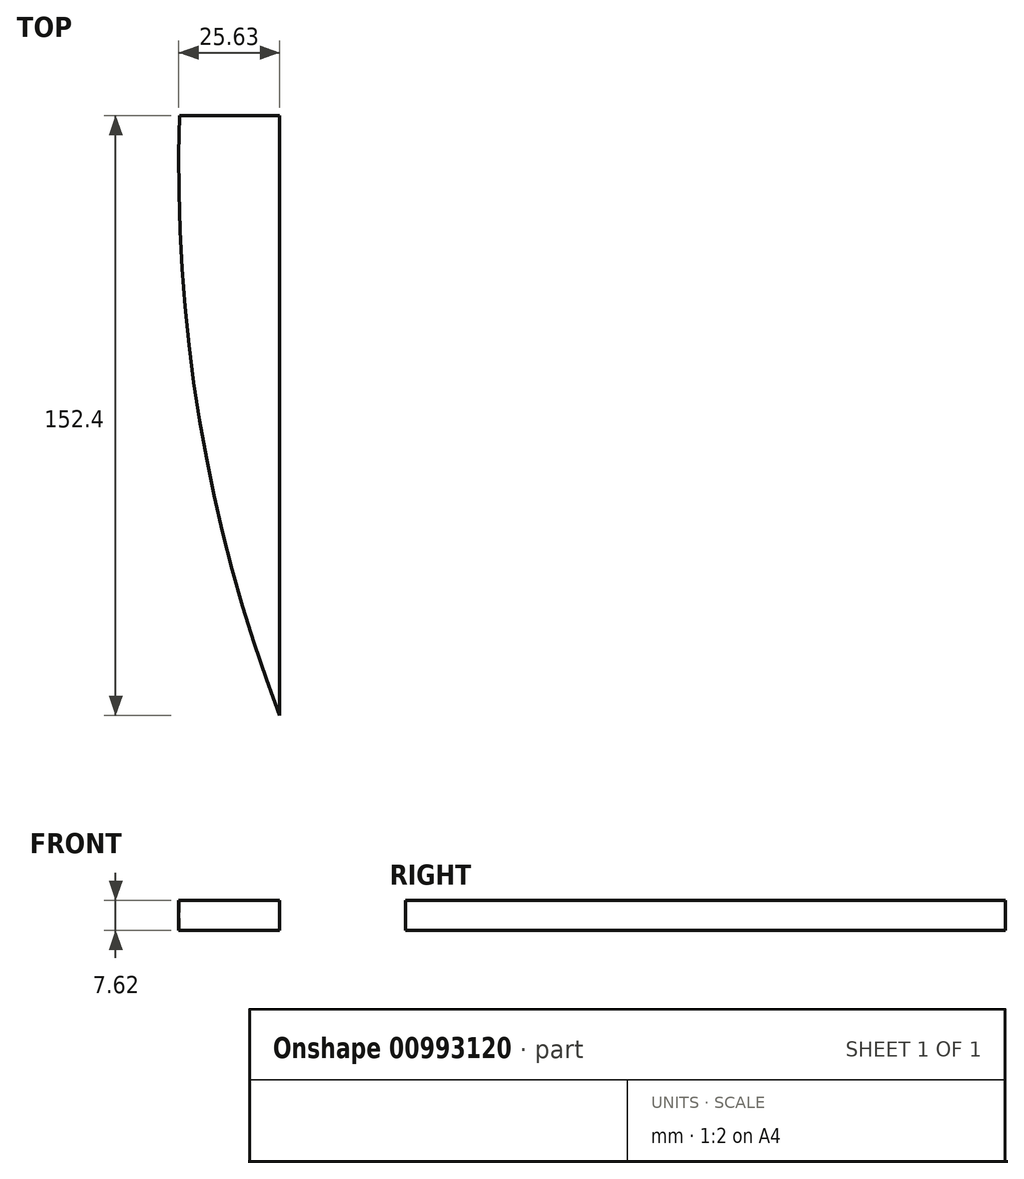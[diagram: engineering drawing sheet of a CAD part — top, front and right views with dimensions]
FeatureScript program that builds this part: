
annotation { "Feature Type Name" : "Feature", "Feature Type Description" : "" }
export const myFeature = defineFeature(function(context is Context, id is Id, definition is map)
    precondition{}
    {
        {
            var Q0;
            Q0=qCreatedBy(makeId("Top.planeOp"),FACE);
            var sketch = newSketch(context, id + "F0", { "sketchPlane" : qUnion([Q0])});
            skLineSegment(sketch, "E0", {"start": v(-32, 38.8) * mm, "end": v(-32, -113.6) * mm});
            skLineSegment(sketch, "E1", {"start": v(-32, 38.8) * mm, "end": v(-57.4, 38.8) * mm});
            skArc(sketch, "E2", {"start": v(-57.4, 38.8) * mm, "mid": v(-52.33, -38.68) * mm, "end": v(-32, -113.6) * mm});
            skSolve(sketch);
        }
        {
            var Q0;
            Q0=makeQuery(id+"F0.imprint","IMPRINT",FACE,{"disambiguationData":[TD([[makeQuery(id+"F0.imprint","IMPRINT",EDGE,{"derivedFrom":sQuery(id+"F0.wireOp",EDGE,"E0")}),-1.0]])]});
            extrude(context, id + "F1", {"entities" : qUnion([Q0]), "depth" : 7.62 * mm, "offsetDistance" : 25.4 * mm});
        }
    });
